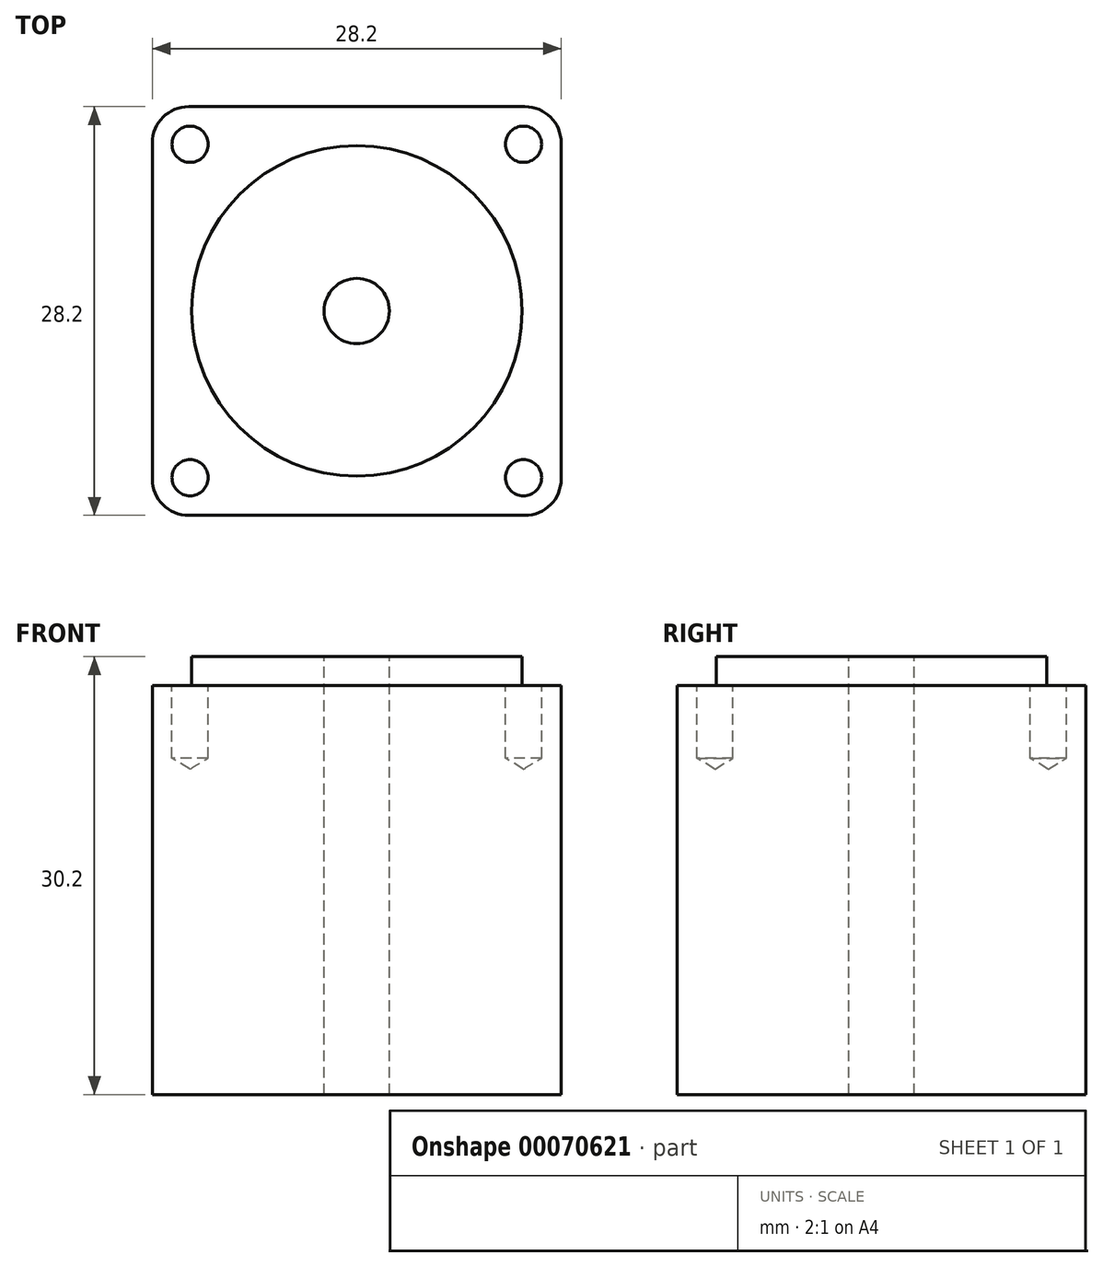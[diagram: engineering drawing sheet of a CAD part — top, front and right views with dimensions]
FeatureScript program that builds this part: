
annotation { "Feature Type Name" : "Feature", "Feature Type Description" : "" }
export const myFeature = defineFeature(function(context is Context, id is Id, definition is map)
    precondition{}
    {
        {
            var Q0;
            Q0=qCreatedBy(makeId("Top.planeOp"),FACE);
            var sketch = newSketch(context, id + "F0", { "sketchPlane" : qUnion([Q0])});
            skLineSegment(sketch, "E0.rect.bottom", {"start": v(14.1, -14.1) * mm, "end": v(-14.1, -14.1) * mm});
            skLineSegment(sketch, "E0.rect.top", {"start": v(14.1, 14.1) * mm, "end": v(-14.1, 14.1) * mm});
            skLineSegment(sketch, "E0.rect.left", {"start": v(14.1, -14.1) * mm, "end": v(14.1, 14.1) * mm});
            skLineSegment(sketch, "E0.rect.right", {"start": v(-14.1, -14.1) * mm, "end": v(-14.1, 14.1) * mm});
            skPoint(sketch, "E0.rect.middle", {"position": v(0, 0) * mm});
            skCircle(sketch, "E1", {"center": v(0, 0) * mm, "radius": 11.4 * mm});
            skCircle(sketch, "E2", {"center": v(0, 0) * mm, "radius": 2.25 * mm});
            skSolve(sketch);
        }
        {
            var Q0;
            Q0=makeQuery(id+"F0.imprint","IMPRINT",FACE,{"disambiguationData":[TD([[makeQuery(id+"F0.imprint","IMPRINT",EDGE,{"derivedFrom":sQuery(id+"F0.wireOp",EDGE,"E0.rect.bottom")}),-1.0]])]});
            var Q1;
            Q1=makeQuery(id+"F0.imprint","IMPRINT",FACE,{"disambiguationData":[TD([[makeQuery(id+"F0.imprint","IMPRINT",EDGE,{"derivedFrom":sQuery(id+"F0.wireOp",EDGE,"E1")}),1.0]])]});
            extrude(context, id + "F1", {"entities" : qUnion([Q0, Q1]), "oppositeDirection" : true, "depth" : 28.2 * mm});
        }
        {
            var Q0;
            Q0=makeQuery(id+"F0.imprint","IMPRINT",FACE,{"disambiguationData":[TD([[makeQuery(id+"F0.imprint","IMPRINT",EDGE,{"derivedFrom":sQuery(id+"F0.wireOp",EDGE,"E1")}),1.0]])]});
            extrude(context, id + "F2", {"entities" : qUnion([Q0]), "operationType" : NewBodyOperationType.ADD, "depth" : 2 * mm});
        }
        {
            var Q0;
            Q0=makeQuery(id+"F1.opExtrude","SWEPT_EDGE",EDGE,{"disambiguationData":[OSD([sQuery(id+"F0.wireOp",EDGE,"E0.rect.bottom"),sQuery(id+"F0.wireOp",EDGE,"E0.rect.right")])]});
            var Q1;
            Q1=makeQuery(id+"F1.opExtrude","SWEPT_EDGE",EDGE,{"disambiguationData":[OSD([sQuery(id+"F0.wireOp",EDGE,"E0.rect.bottom"),sQuery(id+"F0.wireOp",EDGE,"E0.rect.left")])]});
            var Q2;
            Q2=makeQuery(id+"F1.opExtrude","SWEPT_EDGE",EDGE,{"disambiguationData":[OSD([sQuery(id+"F0.wireOp",EDGE,"E0.rect.top"),sQuery(id+"F0.wireOp",EDGE,"E0.rect.right")])]});
            var Q3;
            Q3=makeQuery(id+"F1.opExtrude","SWEPT_EDGE",EDGE,{"disambiguationData":[OSD([sQuery(id+"F0.wireOp",EDGE,"E0.rect.top"),sQuery(id+"F0.wireOp",EDGE,"E0.rect.left")])]});
            fillet(context, id + "F3", {"entities" : qUnion([Q0, Q1, Q2, Q3]), "radius" : 2.5 * mm, "tangentPropagation" : true, "allowEdgeOverflow" : false});
        }
        {
            var Q0;
            Q0=qCreatedBy(makeId("Top.planeOp"),FACE);
            var sketch = newSketch(context, id + "F4", { "sketchPlane" : qUnion([Q0])});
            skCircle(sketch, "E3", {"center": v(-11.5, 11.5) * mm, "radius": 1.25 * mm});
            skCircle(sketch, "E4.1.0.0", {"center": v(11.5, 11.5) * mm, "radius": 1.25 * mm});
            skLineSegment(sketch, "E4.direction1", {"start": v(-11.5, 11.5) * mm, "end": v(11.5, 11.5) * mm, "construction": true});
            skCircle(sketch, "E5.MirrorC", {"center": v(-11.5, -11.5) * mm, "radius": 1.25 * mm});
            skCircle(sketch, "E6.MirrorC", {"center": v(11.5, -11.5) * mm, "radius": 1.25 * mm});
            skSolve(sketch);
        }
        {
            var Q0;
            Q0=sQuery(id+"F4.wireOp",VERTEX,"E3.center");
            var Q1;
            Q1=sQuery(id+"F4.wireOp",VERTEX,"E4.direction1.end");
            var Q2;
            Q2=sQuery(id+"F4.wireOp",VERTEX,"E6.MirrorC.center");
            var Q3;
            Q3=sQuery(id+"F4.wireOp",VERTEX,"E5.MirrorC.center");
            var Q4;
            Q4=makeQuery(id+"F1.opExtrude","SWEPT_BODY",BODY,{"disambiguationData":[OSD([sQuery(id+"F0.wireOp",EDGE,"E0.rect.bottom"),sQuery(id+"F0.wireOp",EDGE,"E0.rect.top"),sQuery(id+"F0.wireOp",EDGE,"E0.rect.left"),sQuery(id+"F0.wireOp",EDGE,"E0.rect.right"),sQuery(id+"F0.wireOp",EDGE,"E2")])]});
            hole(context, id + "F5", {"style" : HoleStyle.SIMPLE, "holeDiameter" : 2.5 * mm, "endStyle" : HoleEndStyle.BLIND, "holeDepth" : 5 * mm, "locations" : qUnion([Q0, Q1, Q2, Q3]), "scope" : qUnion([Q4])});
        }
    });
